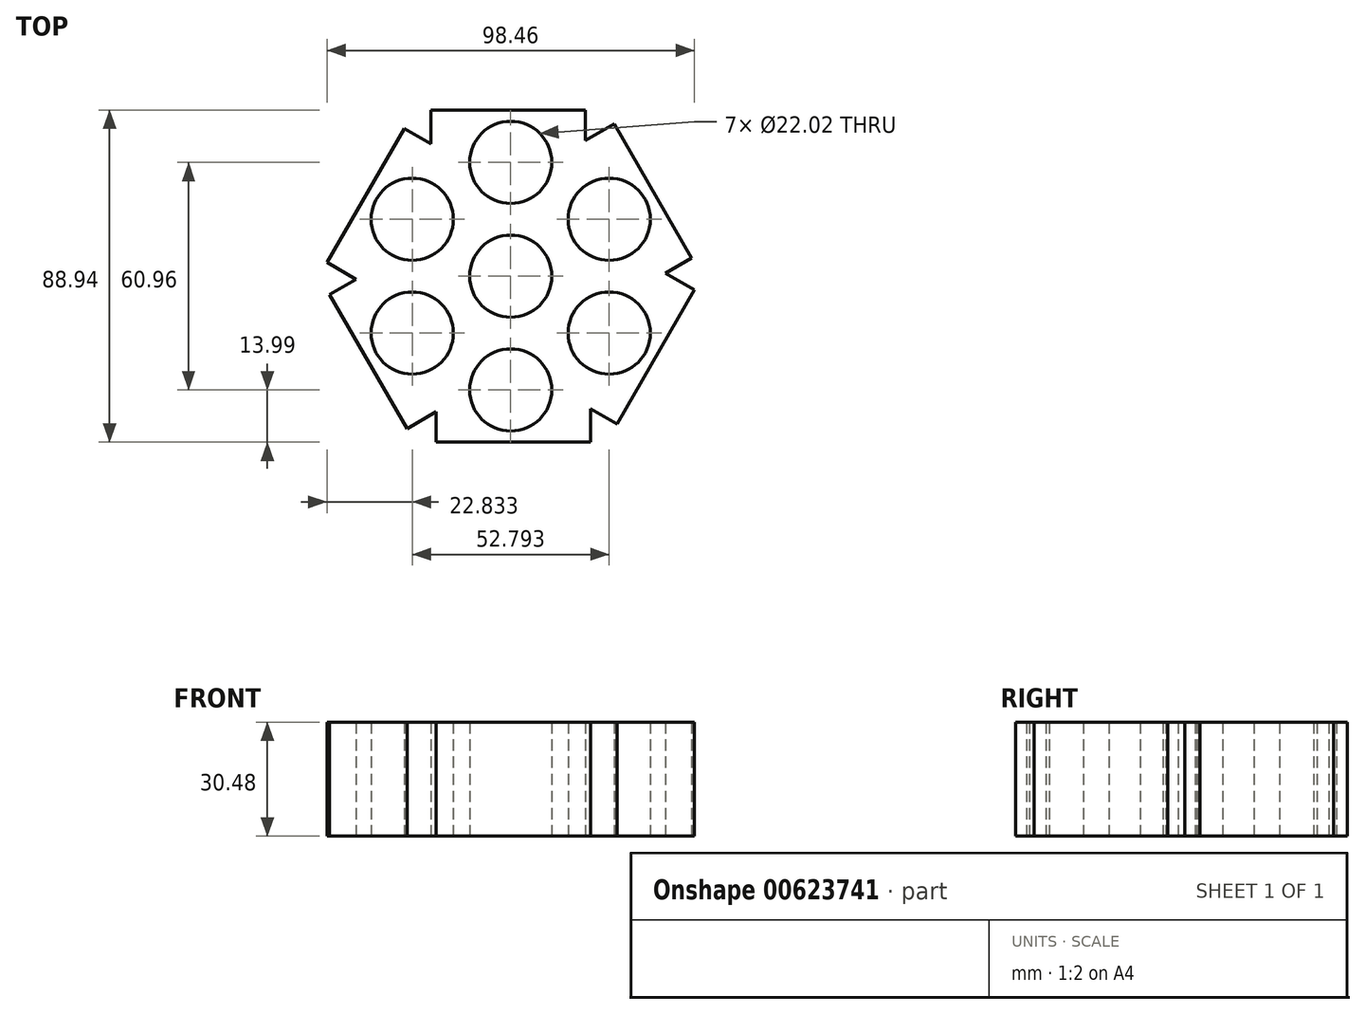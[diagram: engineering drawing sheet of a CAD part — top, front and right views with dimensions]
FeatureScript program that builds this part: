
annotation { "Feature Type Name" : "Feature", "Feature Type Description" : "" }
export const myFeature = defineFeature(function(context is Context, id is Id, definition is map)
    precondition{}
    {
        {
            var Q0;
            Q0=qCreatedBy(makeId("Top.planeOp"),FACE);
            var sketch = newSketch(context, id + "F0", { "sketchPlane" : qUnion([Q0])});
            skCircle(sketch, "E0", {"center": v(0, 0) * mm, "radius": 11.01 * mm});
            skLineSegment(sketch, "E1", {"start": v(0, 0) * mm, "end": v(0, 30.48) * mm});
            skCircle(sketch, "E2", {"center": v(0, 30.48) * mm, "radius": 11.01 * mm});
            skLineSegment(sketch, "E3", {"start": v(-21.44, 21.44) * mm, "end": v(-21.44, 44.47) * mm});
            skLineSegment(sketch, "E4", {"start": v(-21.44, 44.47) * mm, "end": v(20, 44.47) * mm});
            skLineSegment(sketch, "E5", {"start": v(20, 44.47) * mm, "end": v(20, 21.44) * mm});
            skLineSegment(sketch, "E6.1.3.0", {"start": v(21.44, -44.47) * mm, "end": v(-20, -44.47) * mm});
            skLineSegment(sketch, "E6.3.3.0", {"start": v(21.44, -21.44) * mm, "end": v(21.44, -44.47) * mm});
            skLineSegment(sketch, "E6.6.3.0", {"start": v(-20, -44.47) * mm, "end": v(-20, -21.44) * mm});
            skLineSegment(sketch, "E6.1.4.0", {"start": v(49.23, -3.66) * mm, "end": v(28.5, -39.56) * mm});
            skLineSegment(sketch, "E6.3.4.0", {"start": v(29.29, 7.85) * mm, "end": v(49.23, -3.66) * mm});
            skLineSegment(sketch, "E6.6.4.0", {"start": v(28.5, -39.56) * mm, "end": v(8.57, -28.04) * mm});
            skLineSegment(sketch, "E6.1.5.0", {"start": v(27.79, 40.8) * mm, "end": v(48.5, 4.91) * mm});
            skLineSegment(sketch, "E6.3.5.0", {"start": v(7.85, 29.29) * mm, "end": v(27.79, 40.8) * mm});
            skLineSegment(sketch, "E6.6.5.0", {"start": v(48.5, 4.91) * mm, "end": v(28.57, -6.6) * mm});
            skLineSegment(sketch, "E7.1.0", {"start": v(-49.23, 3.66) * mm, "end": v(-28.5, 39.56) * mm});
            skLineSegment(sketch, "E7.1.1", {"start": v(-29.29, -7.85) * mm, "end": v(-49.23, 3.66) * mm});
            skLineSegment(sketch, "E7.1.2", {"start": v(-28.5, 39.56) * mm, "end": v(-8.57, 28.04) * mm});
            skCircle(sketch, "E7.1.3", {"center": v(-26.4, 15.24) * mm, "radius": 11.01 * mm});
            skLineSegment(sketch, "E7.1.4", {"start": v(0, 0) * mm, "end": v(-26.4, 15.24) * mm});
            skLineSegment(sketch, "E7.2.0", {"start": v(-27.79, -40.8) * mm, "end": v(-48.5, -4.91) * mm});
            skLineSegment(sketch, "E7.2.1", {"start": v(-7.85, -29.29) * mm, "end": v(-27.79, -40.8) * mm});
            skLineSegment(sketch, "E7.2.2", {"start": v(-48.5, -4.91) * mm, "end": v(-28.57, 6.6) * mm});
            skCircle(sketch, "E7.2.3", {"center": v(-26.4, -15.24) * mm, "radius": 11.01 * mm});
            skLineSegment(sketch, "E7.2.4", {"start": v(0, 0) * mm, "end": v(-26.4, -15.24) * mm});
            skCircle(sketch, "E7.3.3", {"center": v(0, -30.48) * mm, "radius": 11.01 * mm});
            skLineSegment(sketch, "E7.3.4", {"start": v(0, 0) * mm, "end": v(0, -30.48) * mm});
            skCircle(sketch, "E7.4.3", {"center": v(26.4, -15.24) * mm, "radius": 11.01 * mm});
            skLineSegment(sketch, "E7.4.4", {"start": v(0, 0) * mm, "end": v(26.4, -15.24) * mm});
            skCircle(sketch, "E7.5.3", {"center": v(26.4, 15.24) * mm, "radius": 11.01 * mm});
            skLineSegment(sketch, "E7.5.4", {"start": v(0, 0) * mm, "end": v(26.4, 15.24) * mm});
            skSolve(sketch);
        }
        {
            var Q0;
            Q0 = qSketchRegion(id + "F0", true);
            extrude(context, id + "F1", {"entities" : qUnion([Q0]), "depth" : 30.48 * mm, "offsetDistance" : 25.4 * mm});
        }
    });
